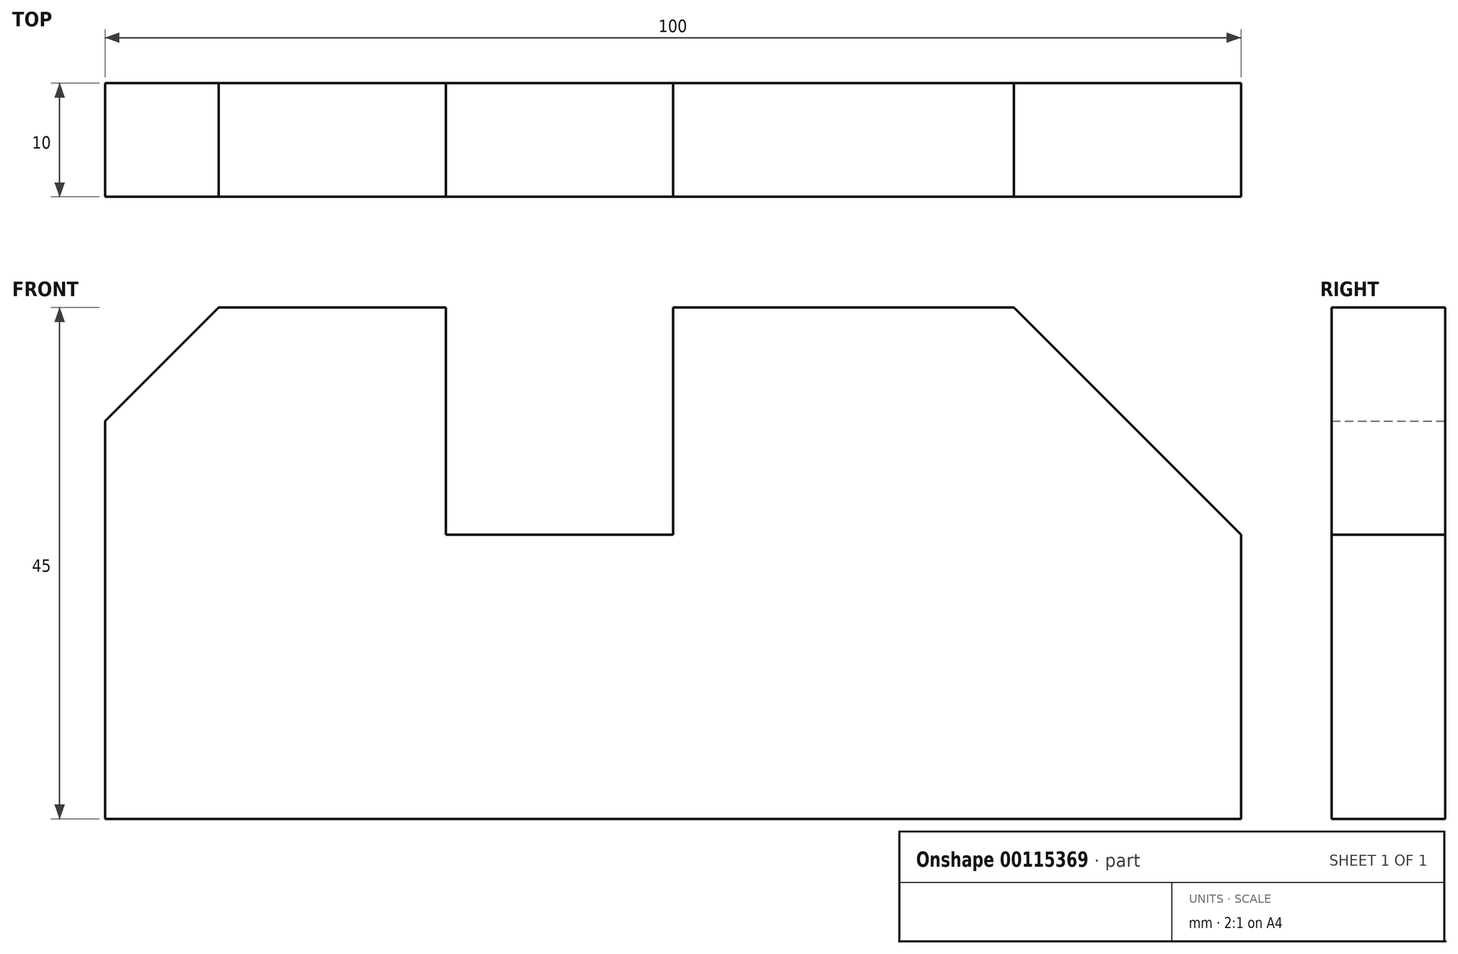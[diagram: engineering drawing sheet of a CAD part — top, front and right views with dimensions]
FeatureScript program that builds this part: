
annotation { "Feature Type Name" : "Feature", "Feature Type Description" : "" }
export const myFeature = defineFeature(function(context is Context, id is Id, definition is map)
    precondition{}
    {
        {
            var Q0;
            Q0=qCreatedBy(makeId("Front.planeOp"),FACE);
            var sketch = newSketch(context, id + "F0", { "sketchPlane" : qUnion([Q0])});
            skLineSegment(sketch, "E0", {"start": v(0, 0) * mm, "end": v(0, 35) * mm});
            skLineSegment(sketch, "E1", {"start": v(0, 35) * mm, "end": v(10, 45) * mm});
            skLineSegment(sketch, "E2", {"start": v(10, 45) * mm, "end": v(30, 45) * mm});
            skLineSegment(sketch, "E3", {"start": v(30, 45) * mm, "end": v(30, 25) * mm});
            skLineSegment(sketch, "E4", {"start": v(30, 25) * mm, "end": v(50, 25) * mm});
            skLineSegment(sketch, "E5", {"start": v(50, 25) * mm, "end": v(50, 45) * mm});
            skLineSegment(sketch, "E6", {"start": v(50, 45) * mm, "end": v(80, 45) * mm});
            skLineSegment(sketch, "E7", {"start": v(80, 45) * mm, "end": v(100, 25) * mm});
            skLineSegment(sketch, "E8", {"start": v(100, 25) * mm, "end": v(100, 0) * mm});
            skLineSegment(sketch, "E9", {"start": v(100, 0) * mm, "end": v(0, 0) * mm});
            skLineSegment(sketch, "E10", {"start": v(0, 45) * mm, "end": v(152.69, 45) * mm, "construction": true});
            skLineSegment(sketch, "E11", {"start": v(100, 0) * mm, "end": v(100, 75.37) * mm, "construction": true});
            skPoint(sketch, "E11.endSnap0", {"position": v(100, 12.5) * mm});
            skLineSegment(sketch, "E12", {"start": v(0, 0) * mm, "end": v(0, 77.86) * mm, "construction": true});
            skSolve(sketch);
        }
        {
            var Q0;
            Q0=makeQuery(id+"F0.imprint","IMPRINT",FACE,{"disambiguationData":[TD([[makeQuery(id+"F0.imprint","IMPRINT",EDGE,{"derivedFrom":sQuery(id+"F0.wireOp",EDGE,"E0")}),-1.0]])]});
            extrude(context, id + "F1", {"entities" : qUnion([Q0]), "depth" : 10 * mm});
        }
    });
